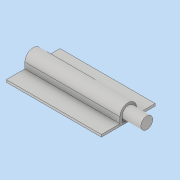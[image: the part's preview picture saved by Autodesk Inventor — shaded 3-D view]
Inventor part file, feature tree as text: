
AUTODESK INVENTOR PART (.ipt)
format: ipt  version: 2019 (Build 230136000, 136)  size: 143,872 bytes
history: native  units: mm
features: other x5, extrude x3, projected_geometry x1
ambient origin geometry x8: Origin, YZ Plane, XZ Plane, XY Plane, X Axis, Y Axis, Z Axis, Center Point
bodies: Body1 (feature_tree)
feature tree (9):
  other  "<userpath>\source\LW2021\LW_SAPR\parametres.xlsx"
  other  "Твердое тело1"
  extrude  "Выдавливание1"  Depth=10.0mm
  extrude  "Выдавливание2"  Depth=80.0mm TaperAngle=0.0deg
  extrude  "Выдавливание3"  Depth=80.0mm TaperAngle=0.0deg
  other  "Цилиндр"
  other  "Корпус"
  other  "Выемка"
  projected_geometry  "Спроецированная петля3"
